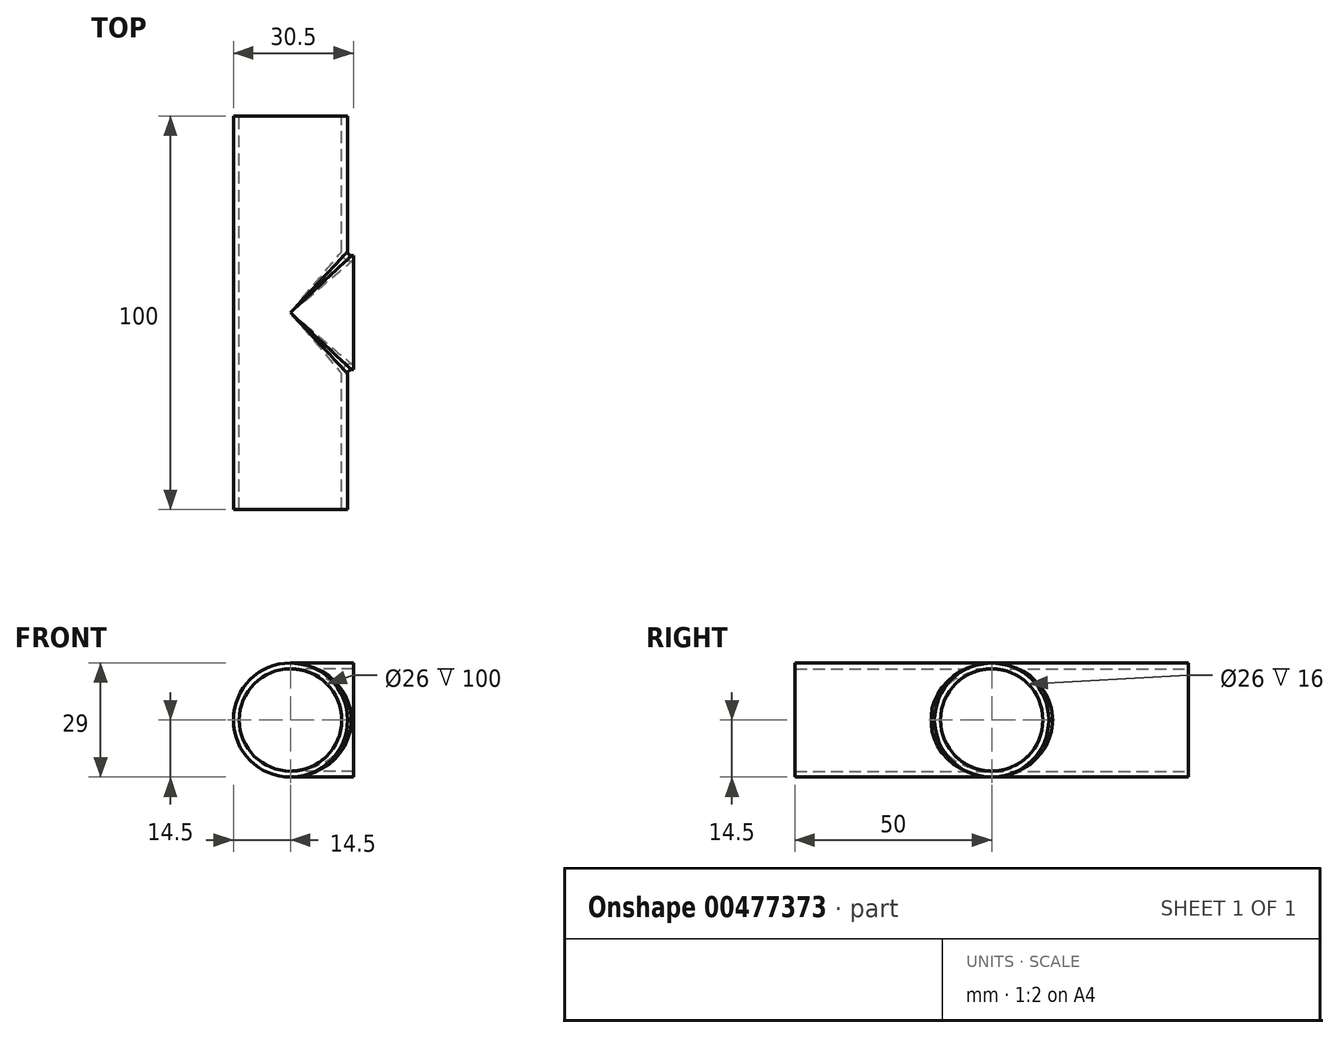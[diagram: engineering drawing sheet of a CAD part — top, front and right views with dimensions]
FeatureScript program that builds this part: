
annotation { "Feature Type Name" : "Feature", "Feature Type Description" : "" }
export const myFeature = defineFeature(function(context is Context, id is Id, definition is map)
    precondition{}
    {
        {
            var Q0;
            Q0=qCreatedBy(makeId("Front.planeOp"),FACE);
            var sketch = newSketch(context, id + "F0", { "sketchPlane" : qUnion([Q0])});
            skCircle(sketch, "E0", {"center": v(0, 0) * mm, "radius": 14.5 * mm});
            skSolve(sketch);
        }
        {
            var Q0;
            Q0 = qSketchRegion(id + "F0", true);
            extrude(context, id + "F1", {"entities" : qUnion([Q0]), "depth" : 50 * mm, "hasSecondDirection" : true, "secondDirectionOppositeDirection" : true, "secondDirectionDepth" : 50 * mm});
        }
        {
            var Q0;
            Q0=qCreatedBy(makeId("Right.planeOp"),FACE);
            var sketch = newSketch(context, id + "F2", { "sketchPlane" : qUnion([Q0])});
            skCircle(sketch, "E1", {"center": v(0, 0) * mm, "radius": 14.5 * mm});
            skSolve(sketch);
        }
        {
            var Q0;
            Q0 = qSketchRegion(id + "F2", true);
            extrude(context, id + "F3", {"entities" : qUnion([Q0]), "operationType" : NewBodyOperationType.ADD, "depth" : 16 * mm});
        }
        {
            var Q0;
            Q0=makeQuery(id+"F3.boolean.opBoolean","INTERSECT",EDGE,{"disambiguationData":[OD(0.0)],"derivedFrom":[makeQuery(id+"F1.opExtrude","SWEPT_FACE",FACE,{"disambiguationData":[OSD([sQuery(id+"F0.wireOp",EDGE,"E0")])]}),makeQuery(id+"F3.opExtrude","SWEPT_FACE",FACE,{"disambiguationData":[OSD([sQuery(id+"F2.wireOp",EDGE,"E1")])]})]});
            var Q1;
            Q1=makeQuery(id+"F3.boolean.opBoolean","INTERSECT",EDGE,{"disambiguationData":[OD(1.0)],"derivedFrom":[makeQuery(id+"F1.opExtrude","SWEPT_FACE",FACE,{"disambiguationData":[OSD([sQuery(id+"F0.wireOp",EDGE,"E0")])]}),makeQuery(id+"F3.opExtrude","SWEPT_FACE",FACE,{"disambiguationData":[OSD([sQuery(id+"F2.wireOp",EDGE,"E1")])]})]});
            fillet(context, id + "F4", {"entities" : qUnion([Q0, Q1]), "radius" : 1 * mm, "tangentPropagation" : true, "allowEdgeOverflow" : false});
        }
        {
            var Q0;
            Q0=makeQuery(id+"F1.opExtrude","CAP_FACE",FACE,{"disambiguationData":[OSD([sQuery(id+"F0.wireOp",EDGE,"E0")])],"isStart":false});
            var Q1;
            Q1=makeQuery(id+"F3.opExtrude","CAP_FACE",FACE,{"disambiguationData":[OSD([sQuery(id+"F2.wireOp",EDGE,"E1")])],"isStart":false});
            var Q2;
            Q2=makeQuery(id+"F1.opExtrude","CAP_FACE",FACE,{"disambiguationData":[OSD([sQuery(id+"F0.wireOp",EDGE,"E0")])],"isStart":true});
            shell(context, id + "F5", {"entities" : qUnion([Q0, Q1, Q2]), "thickness" : 1.5 * mm});
        }
    });
